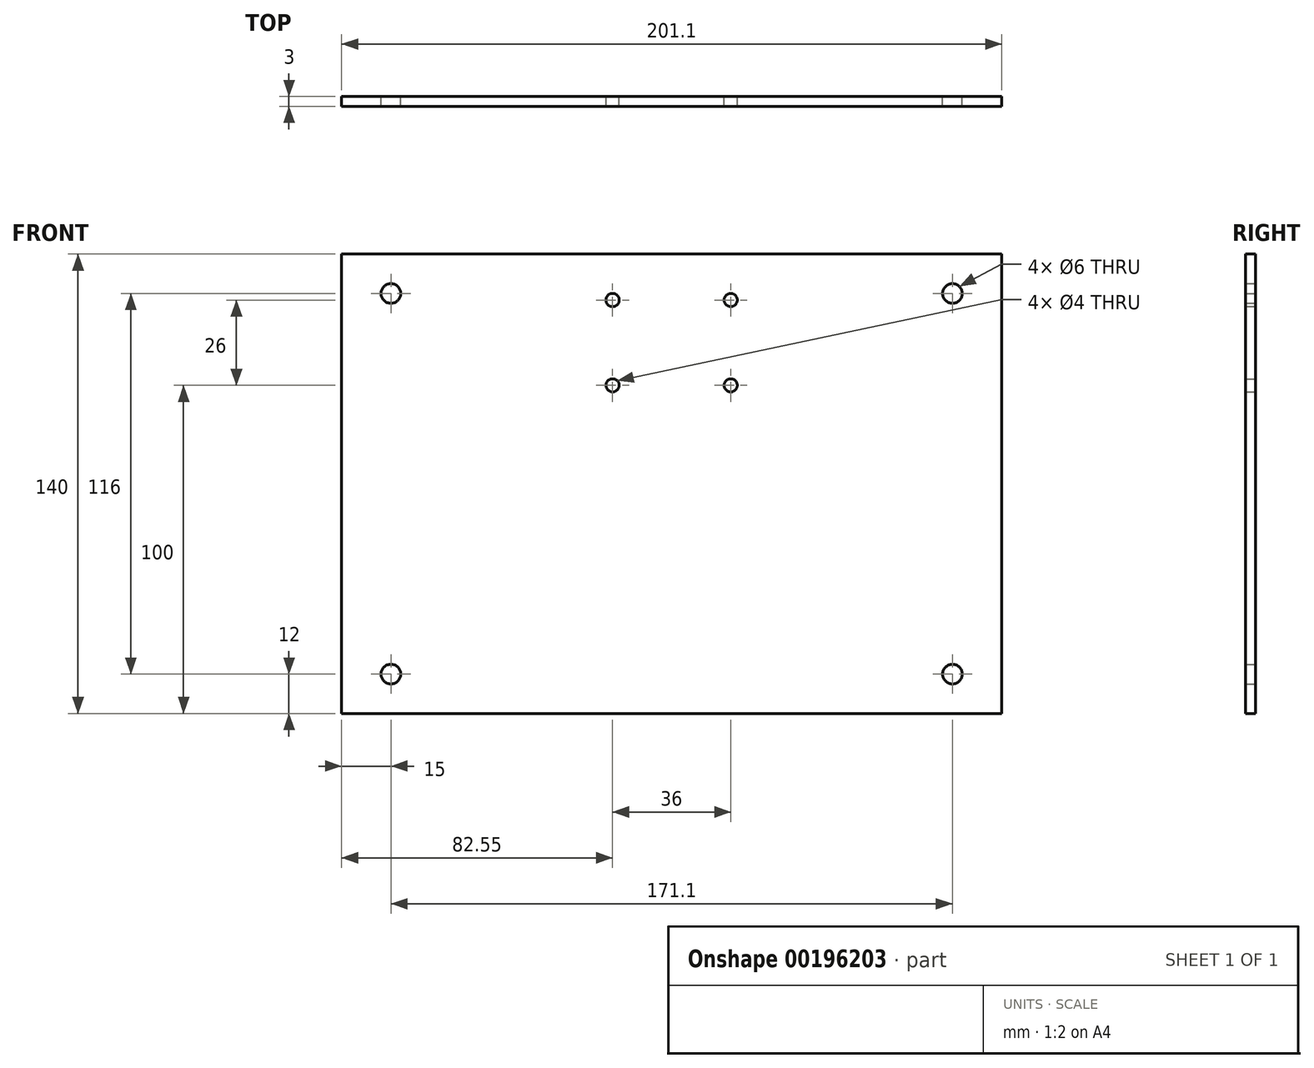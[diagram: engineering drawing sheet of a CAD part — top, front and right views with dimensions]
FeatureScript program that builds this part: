
annotation { "Feature Type Name" : "Feature", "Feature Type Description" : "" }
export const myFeature = defineFeature(function(context is Context, id is Id, definition is map)
    precondition{}
    {
        {
            var Q0;
            Q0=qCreatedBy(makeId("Front.planeOp"),FACE);
            var sketch = newSketch(context, id + "F0", { "sketchPlane" : qUnion([Q0])});
            skLineSegment(sketch, "E0.bottom", {"start": v(100.55, -70) * mm, "end": v(-100.55, -70) * mm});
            skLineSegment(sketch, "E0.top", {"start": v(100.55, 70) * mm, "end": v(-100.55, 70) * mm});
            skLineSegment(sketch, "E0.left", {"start": v(100.55, -70) * mm, "end": v(100.55, 70) * mm});
            skLineSegment(sketch, "E0.right", {"start": v(-100.55, -70) * mm, "end": v(-100.55, 70) * mm});
            skPoint(sketch, "E0.middle", {"position": v(0, 0) * mm});
            skLineSegment(sketch, "E1.0", {"start": v(100.55, 58) * mm, "end": v(-100.55, 58) * mm, "construction": true});
            skLineSegment(sketch, "E2.0", {"start": v(100.55, -58) * mm, "end": v(-100.55, -58) * mm, "construction": true});
            skLineSegment(sketch, "E3.0", {"start": v(-85.55, -70) * mm, "end": v(-85.55, 70) * mm, "construction": true});
            skLineSegment(sketch, "E4.0", {"start": v(85.55, -70) * mm, "end": v(85.55, 70) * mm, "construction": true});
            skCircle(sketch, "E5", {"center": v(-85.55, 58) * mm, "radius": 3 * mm});
            skCircle(sketch, "E6", {"center": v(-85.55, -58) * mm, "radius": 3 * mm});
            skCircle(sketch, "E7", {"center": v(85.55, -58) * mm, "radius": 3 * mm});
            skCircle(sketch, "E8", {"center": v(85.55, 58) * mm, "radius": 3 * mm});
            skLineSegment(sketch, "E9.bottom", {"start": v(18, 30) * mm, "end": v(-18, 30) * mm, "construction": true});
            skLineSegment(sketch, "E9.top", {"start": v(18, 56) * mm, "end": v(-18, 56) * mm, "construction": true});
            skLineSegment(sketch, "E9.left", {"start": v(18, 30) * mm, "end": v(18, 56) * mm, "construction": true});
            skLineSegment(sketch, "E9.right", {"start": v(-18, 30) * mm, "end": v(-18, 56) * mm, "construction": true});
            skPoint(sketch, "E9.middle", {"position": v(0, 43) * mm});
            skCircle(sketch, "E10", {"center": v(-18, 56) * mm, "radius": 2 * mm});
            skCircle(sketch, "E11", {"center": v(-18, 30) * mm, "radius": 2 * mm});
            skCircle(sketch, "E12", {"center": v(18, 56) * mm, "radius": 2 * mm});
            skCircle(sketch, "E13", {"center": v(18, 30) * mm, "radius": 2 * mm});
            skSolve(sketch);
        }
        {
            var Q0;
            Q0 = qSketchRegion(id + "F0", true);
            extrude(context, id + "F1", {"entities" : qUnion([Q0]), "depth" : 3 * mm});
        }
    });
